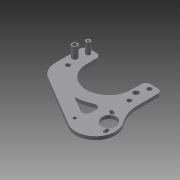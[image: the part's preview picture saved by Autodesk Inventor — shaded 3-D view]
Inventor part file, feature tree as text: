
AUTODESK INVENTOR PART (.ipt)
format: ipt  version: 2015 (Build 190159000, 159)  size: 210,944 bytes
history: native  units: mm
features: reference x14, extrude x2, sketch x2, projected_geometry x1
ambient origin geometry x8: Origin, YZ Plane, XZ Plane, XY Plane, X Axis, Y Axis, Z Axis, Center Point
bodies: Solid1 (feature_tree)
feature tree (19):
  extrude  "Extrusion1"  Depth=3.0mm
  extrude  "Extrusion2"  Depth=10.0mm
  sketch  "Sketch1"  dims[d0=3.0mm d1=0.872665mm]
  reference  "Reference1"
  reference  "Reference2"
  reference  "Reference3"
  reference  "Reference4"
  reference  "Reference5"
  reference  "Reference6"
  reference  "Reference7"
  reference  "Reference8"
  reference  "Reference9"
  reference  "Reference10"
  reference  "Reference11"
  reference  "Reference12"
  reference  "Reference14"
  reference  "Reference15"
  sketch  "Sketch2"  dims[d2=0.872665mm d3=0.872665mm d4=12.5mm d5=3.0mm d6=4.0mm d7=4.0mm d8=5.0mm d9=4.0mm d10=5.0mm d11=4.0mm d12=4.0mm d13=3.0mm d14=0.0mm d15=4.0mm d16=3.5mm d17=2.0mm d18=10.0mm d19=0.0mm]
  projected_geometry  "Projected Loop1"
